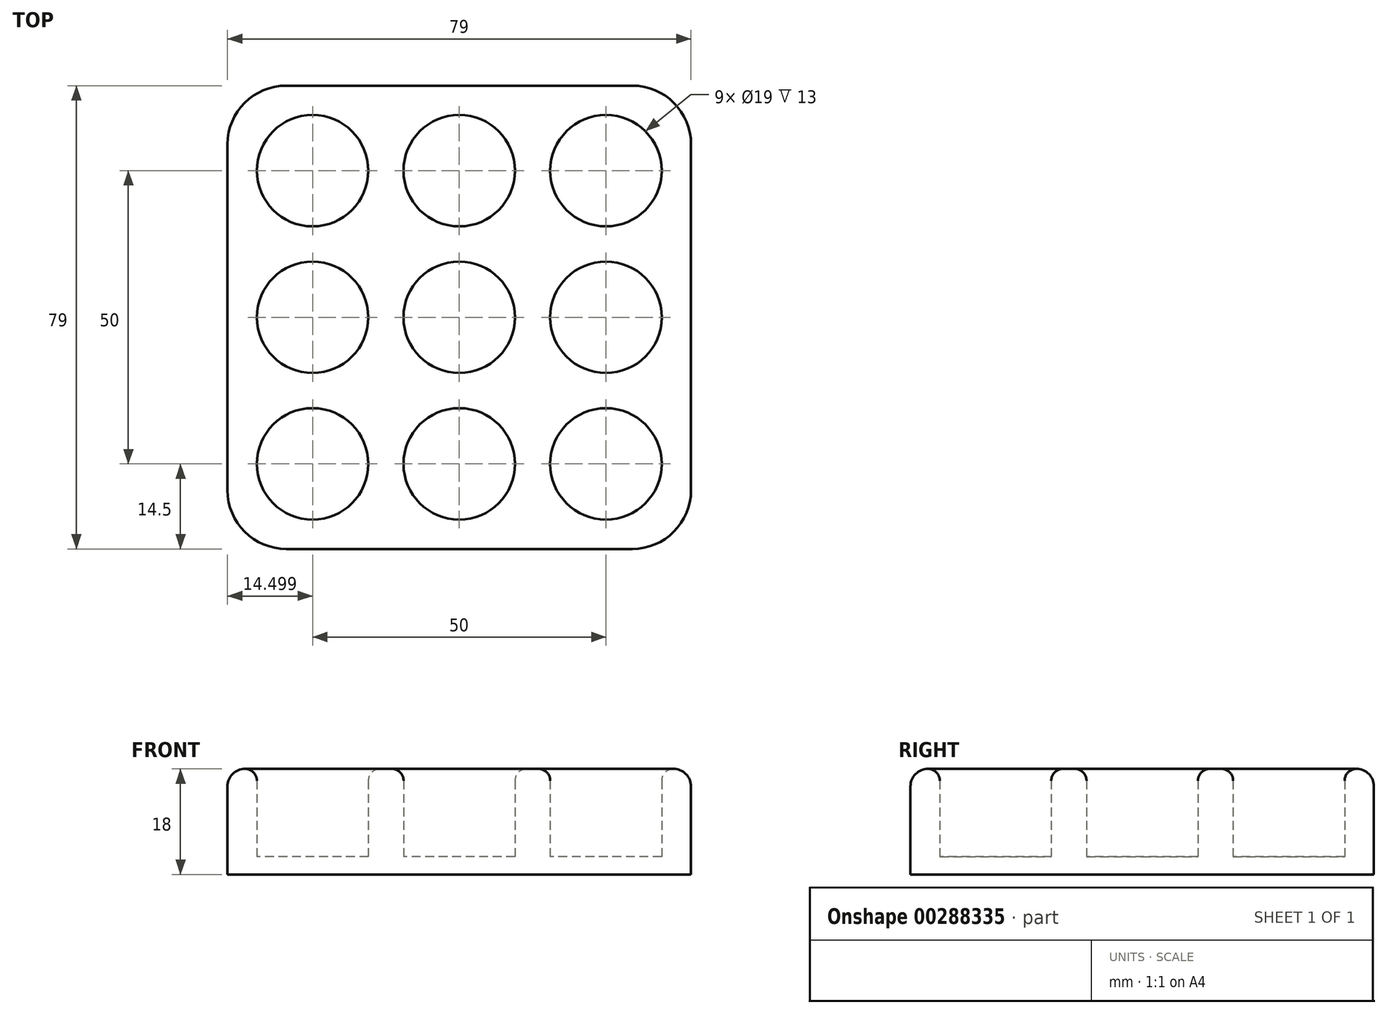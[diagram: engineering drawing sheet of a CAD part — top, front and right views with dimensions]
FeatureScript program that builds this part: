
annotation { "Feature Type Name" : "Feature", "Feature Type Description" : "" }
export const myFeature = defineFeature(function(context is Context, id is Id, definition is map)
    precondition{}
    {
        {
            var Q0;
            Q0=qCreatedBy(makeId("Top.planeOp"),FACE);
            var sketch = newSketch(context, id + "F0", { "sketchPlane" : qUnion([Q0])});
            skCircle(sketch, "E0", {"center": v(-32.91, 14.5) * mm, "radius": 9.5 * mm});
            skCircle(sketch, "E1.0.1.0", {"center": v(-32.91, 39.5) * mm, "radius": 9.5 * mm});
            skCircle(sketch, "E1.0.2.0", {"center": v(-32.91, 64.5) * mm, "radius": 9.5 * mm});
            skCircle(sketch, "E1.1.0.0", {"center": v(-7.91, 14.5) * mm, "radius": 9.5 * mm});
            skCircle(sketch, "E1.1.1.0", {"center": v(-7.91, 39.5) * mm, "radius": 9.5 * mm});
            skCircle(sketch, "E1.1.2.0", {"center": v(-7.91, 64.5) * mm, "radius": 9.5 * mm});
            skCircle(sketch, "E1.2.0.0", {"center": v(17.09, 14.5) * mm, "radius": 9.5 * mm});
            skCircle(sketch, "E1.2.1.0", {"center": v(17.09, 39.5) * mm, "radius": 9.5 * mm});
            skCircle(sketch, "E1.2.2.0", {"center": v(17.09, 64.5) * mm, "radius": 9.5 * mm});
            skLineSegment(sketch, "E1.direction1", {"start": v(-32.91, 14.5) * mm, "end": v(-7.91, 14.5) * mm, "construction": true});
            skLineSegment(sketch, "E1.direction2", {"start": v(-32.91, 14.5) * mm, "end": v(-32.91, 39.5) * mm, "construction": true});
            skLineSegment(sketch, "E2.bottom", {"start": v(-47.41, 79) * mm, "end": v(31.59, 79) * mm});
            skLineSegment(sketch, "E2.top", {"start": v(-47.41, 0) * mm, "end": v(31.59, 0) * mm});
            skLineSegment(sketch, "E2.left", {"start": v(-47.41, 79) * mm, "end": v(-47.41, 0) * mm});
            skLineSegment(sketch, "E2.right", {"start": v(31.59, 79) * mm, "end": v(31.59, 0) * mm});
            skLineSegment(sketch, "E3", {"start": v(26.58, 64.02) * mm, "end": v(26.59, 14.5) * mm, "construction": true});
            skLineSegment(sketch, "E4", {"start": v(16.75, 5) * mm, "end": v(-32.9, 5) * mm, "construction": true});
            skLineSegment(sketch, "E5", {"start": v(-42.4, 14.87) * mm, "end": v(-42.41, 64.5) * mm, "construction": true});
            skLineSegment(sketch, "E6", {"start": v(-32.9, 74) * mm, "end": v(17.09, 74) * mm, "construction": true});
            skSolve(sketch);
        }
        {
            var Q0;
            Q0=makeQuery(id+"F0.imprint","IMPRINT",FACE,{"disambiguationData":[TD([[makeQuery(id+"F0.imprint","IMPRINT",EDGE,{"derivedFrom":sQuery(id+"F0.wireOp",EDGE,"E0")}),-1.0]])]});
            extrude(context, id + "F1", {"entities" : qUnion([Q0]), "depth" : 15 * mm});
        }
        {
            var Q0;
            Q0=makeQuery(id+"F0.imprint","IMPRINT",FACE,{"disambiguationData":[TD([[makeQuery(id+"F0.imprint","IMPRINT",EDGE,{"derivedFrom":sQuery(id+"F0.wireOp",EDGE,"E0")}),-1.0]])]});
            var Q1;
            Q1=makeQuery(id+"F0.imprint","IMPRINT",FACE,{"disambiguationData":[TD([[makeQuery(id+"F0.imprint","IMPRINT",EDGE,{"derivedFrom":sQuery(id+"F0.wireOp",EDGE,"E1.2.2.0")}),1.0]])]});
            var Q2;
            Q2=makeQuery(id+"F0.imprint","IMPRINT",FACE,{"disambiguationData":[TD([[makeQuery(id+"F0.imprint","IMPRINT",EDGE,{"derivedFrom":sQuery(id+"F0.wireOp",EDGE,"E1.1.2.0")}),1.0]])]});
            var Q3;
            Q3=makeQuery(id+"F0.imprint","IMPRINT",FACE,{"disambiguationData":[TD([[makeQuery(id+"F0.imprint","IMPRINT",EDGE,{"derivedFrom":sQuery(id+"F0.wireOp",EDGE,"E1.0.2.0")}),1.0]])]});
            var Q4;
            Q4=makeQuery(id+"F0.imprint","IMPRINT",FACE,{"disambiguationData":[TD([[makeQuery(id+"F0.imprint","IMPRINT",EDGE,{"derivedFrom":sQuery(id+"F0.wireOp",EDGE,"E1.0.1.0")}),1.0]])]});
            var Q5;
            Q5=makeQuery(id+"F0.imprint","IMPRINT",FACE,{"disambiguationData":[TD([[makeQuery(id+"F0.imprint","IMPRINT",EDGE,{"derivedFrom":sQuery(id+"F0.wireOp",EDGE,"E1.1.1.0")}),1.0]])]});
            var Q6;
            Q6=makeQuery(id+"F0.imprint","IMPRINT",FACE,{"disambiguationData":[TD([[makeQuery(id+"F0.imprint","IMPRINT",EDGE,{"derivedFrom":sQuery(id+"F0.wireOp",EDGE,"E1.2.1.0")}),1.0]])]});
            var Q7;
            Q7=makeQuery(id+"F0.imprint","IMPRINT",FACE,{"disambiguationData":[TD([[makeQuery(id+"F0.imprint","IMPRINT",EDGE,{"derivedFrom":sQuery(id+"F0.wireOp",EDGE,"E1.2.0.0")}),1.0]])]});
            var Q8;
            Q8=makeQuery(id+"F0.imprint","IMPRINT",FACE,{"disambiguationData":[TD([[makeQuery(id+"F0.imprint","IMPRINT",EDGE,{"derivedFrom":sQuery(id+"F0.wireOp",EDGE,"E1.1.0.0")}),1.0]])]});
            var Q9;
            Q9=makeQuery(id+"F0.imprint","IMPRINT",FACE,{"disambiguationData":[TD([[makeQuery(id+"F0.imprint","IMPRINT",EDGE,{"derivedFrom":sQuery(id+"F0.wireOp",EDGE,"E0")}),1.0]])]});
            extrude(context, id + "F2", {"entities" : qUnion([Q0, Q1, Q2, Q3, Q4, Q5, Q6, Q7, Q8, Q9]), "operationType" : NewBodyOperationType.ADD, "oppositeDirection" : true, "depth" : 3 * mm});
        }
        {
            var Q0;
            Q0=makeQuery(id+"F1.opExtrude","CAP_EDGE",EDGE,{"disambiguationData":[OSD([sQuery(id+"F0.wireOp",EDGE,"E2.left")])],"isStart":false});
            var Q1;
            Q1=makeQuery(id+"F1.opExtrude","CAP_EDGE",EDGE,{"disambiguationData":[OSD([sQuery(id+"F0.wireOp",EDGE,"E2.bottom")])],"isStart":false});
            var Q2;
            Q2=makeQuery(id+"F1.opExtrude","CAP_EDGE",EDGE,{"disambiguationData":[OSD([sQuery(id+"F0.wireOp",EDGE,"E2.right")])],"isStart":false});
            var Q3;
            Q3=makeQuery(id+"F1.opExtrude","CAP_EDGE",EDGE,{"disambiguationData":[OSD([sQuery(id+"F0.wireOp",EDGE,"E2.top")])],"isStart":false});
            fillet(context, id + "F3", {"entities" : qUnion([Q0, Q1, Q2, Q3]), "radius" : 3 * mm, "tangentPropagation" : true, "allowEdgeOverflow" : false});
        }
        {
            var Q0;
            Q0=makeQuery(id+"F1.opExtrude","CAP_EDGE",EDGE,{"disambiguationData":[OSD([sQuery(id+"F0.wireOp",EDGE,"E1.0.2.0")])],"isStart":false});
            var Q1;
            Q1=makeQuery(id+"F1.opExtrude","CAP_EDGE",EDGE,{"disambiguationData":[OSD([sQuery(id+"F0.wireOp",EDGE,"E1.1.2.0")])],"isStart":false});
            var Q2;
            Q2=makeQuery(id+"F1.opExtrude","CAP_EDGE",EDGE,{"disambiguationData":[OSD([sQuery(id+"F0.wireOp",EDGE,"E1.2.2.0")])],"isStart":false});
            var Q3;
            Q3=makeQuery(id+"F1.opExtrude","CAP_EDGE",EDGE,{"disambiguationData":[OSD([sQuery(id+"F0.wireOp",EDGE,"E1.2.1.0")])],"isStart":false});
            var Q4;
            Q4=makeQuery(id+"F1.opExtrude","CAP_EDGE",EDGE,{"disambiguationData":[OSD([sQuery(id+"F0.wireOp",EDGE,"E1.2.0.0")])],"isStart":false});
            var Q5;
            Q5=makeQuery(id+"F1.opExtrude","CAP_EDGE",EDGE,{"disambiguationData":[OSD([sQuery(id+"F0.wireOp",EDGE,"E1.1.0.0")])],"isStart":false});
            var Q6;
            Q6=makeQuery(id+"F1.opExtrude","CAP_EDGE",EDGE,{"disambiguationData":[OSD([sQuery(id+"F0.wireOp",EDGE,"E1.1.1.0")])],"isStart":false});
            var Q7;
            Q7=makeQuery(id+"F1.opExtrude","CAP_EDGE",EDGE,{"disambiguationData":[OSD([sQuery(id+"F0.wireOp",EDGE,"E1.0.1.0")])],"isStart":false});
            var Q8;
            Q8=makeQuery(id+"F1.opExtrude","CAP_EDGE",EDGE,{"disambiguationData":[OSD([sQuery(id+"F0.wireOp",EDGE,"E0")])],"isStart":false});
            fillet(context, id + "F4", {"entities" : qUnion([Q0, Q1, Q2, Q3, Q4, Q5, Q6, Q7, Q8]), "radius" : 2 * mm, "tangentPropagation" : true, "allowEdgeOverflow" : false});
        }
        {
            var Q0;
            {var subQ0=sQuery(id+"F0.wireOp",EDGE,"E2.left");var subQ1=sQuery(id+"F0.wireOp",EDGE,"E2.bottom");Q0=makeQuery(id+"F2.boolean.opBoolean","MERGE",EDGE,{"derivedFrom":[makeQuery(id+"F1.opExtrude","SWEPT_EDGE",EDGE,{"disambiguationData":[OSD([subQ1,subQ0])]}),makeQuery(id+"F2.opExtrude","SWEPT_EDGE",EDGE,{"disambiguationData":[OSD([subQ1,subQ0])]})]});}
            var Q1;
            {var subQ0=sQuery(id+"F0.wireOp",EDGE,"E2.right");var subQ1=sQuery(id+"F0.wireOp",EDGE,"E2.bottom");Q1=makeQuery(id+"F2.boolean.opBoolean","MERGE",EDGE,{"derivedFrom":[makeQuery(id+"F1.opExtrude","SWEPT_EDGE",EDGE,{"disambiguationData":[OSD([subQ1,subQ0])]}),makeQuery(id+"F2.opExtrude","SWEPT_EDGE",EDGE,{"disambiguationData":[OSD([subQ1,subQ0])]})]});}
            var Q2;
            {var subQ0=sQuery(id+"F0.wireOp",EDGE,"E2.right");var subQ1=sQuery(id+"F0.wireOp",EDGE,"E2.top");Q2=makeQuery(id+"F2.boolean.opBoolean","MERGE",EDGE,{"derivedFrom":[makeQuery(id+"F1.opExtrude","SWEPT_EDGE",EDGE,{"disambiguationData":[OSD([subQ1,subQ0])]}),makeQuery(id+"F2.opExtrude","SWEPT_EDGE",EDGE,{"disambiguationData":[OSD([subQ1,subQ0])]})]});}
            var Q3;
            {var subQ0=sQuery(id+"F0.wireOp",EDGE,"E2.left");var subQ1=sQuery(id+"F0.wireOp",EDGE,"E2.top");Q3=makeQuery(id+"F2.boolean.opBoolean","MERGE",EDGE,{"derivedFrom":[makeQuery(id+"F1.opExtrude","SWEPT_EDGE",EDGE,{"disambiguationData":[OSD([subQ1,subQ0])]}),makeQuery(id+"F2.opExtrude","SWEPT_EDGE",EDGE,{"disambiguationData":[OSD([subQ1,subQ0])]})]});}
            fillet(context, id + "F5", {"entities" : qUnion([Q0, Q1, Q2, Q3]), "radius" : 10 * mm, "tangentPropagation" : true, "allowEdgeOverflow" : false});
        }
    });
